# Revit family: rba-bim-rba1211 Series
name_source: partatom
category: Plumbing Fixtures
revit_build: Autodesk Revit 2018 (Build: 20170223_1515(x64)
units: mm (PartAtom-declared; Revit-internal decimal feet)

## family parameters
Always vertical = Yes
Cut with Voids When Loaded = No
OmniClass Number = 23.45.55.14
OmniClass Title = Single Faucets
Part Type = Normal
Room Calculation Point = No
Round Connector Dimension = Use Radius
Shared = No
Work Plane-Based = No

## types (3) — shared parameters
Manufacturer = RBA Group
Materials and Finishes = Polished Chrome Finish
Modified Issue = 20200925.01
RADIUS = 29.5 mm

## per-type parameters (varying)
| type | Description | URL |
| RBA1211-600-001 | Formatta 6 Star Single Temp Sensor Tap, Mains powered, 20 seconds preset | http://www.rba.com.au |
| RBA1211-600 | Formatta 6 Star Single Temp Sensor Tap, Mains powered | www.rba.com.au |
| RBA1211-613 | Formatta 6 Star Single Temp Sensor Tap, Battery powered | www.rba.com.au |

note: column(s) folded — value = type name in every type: Model

## geometry (parser evidence)
native form markers: Blend x2, Sweep x3
no freeform markers — native parametric forms only
